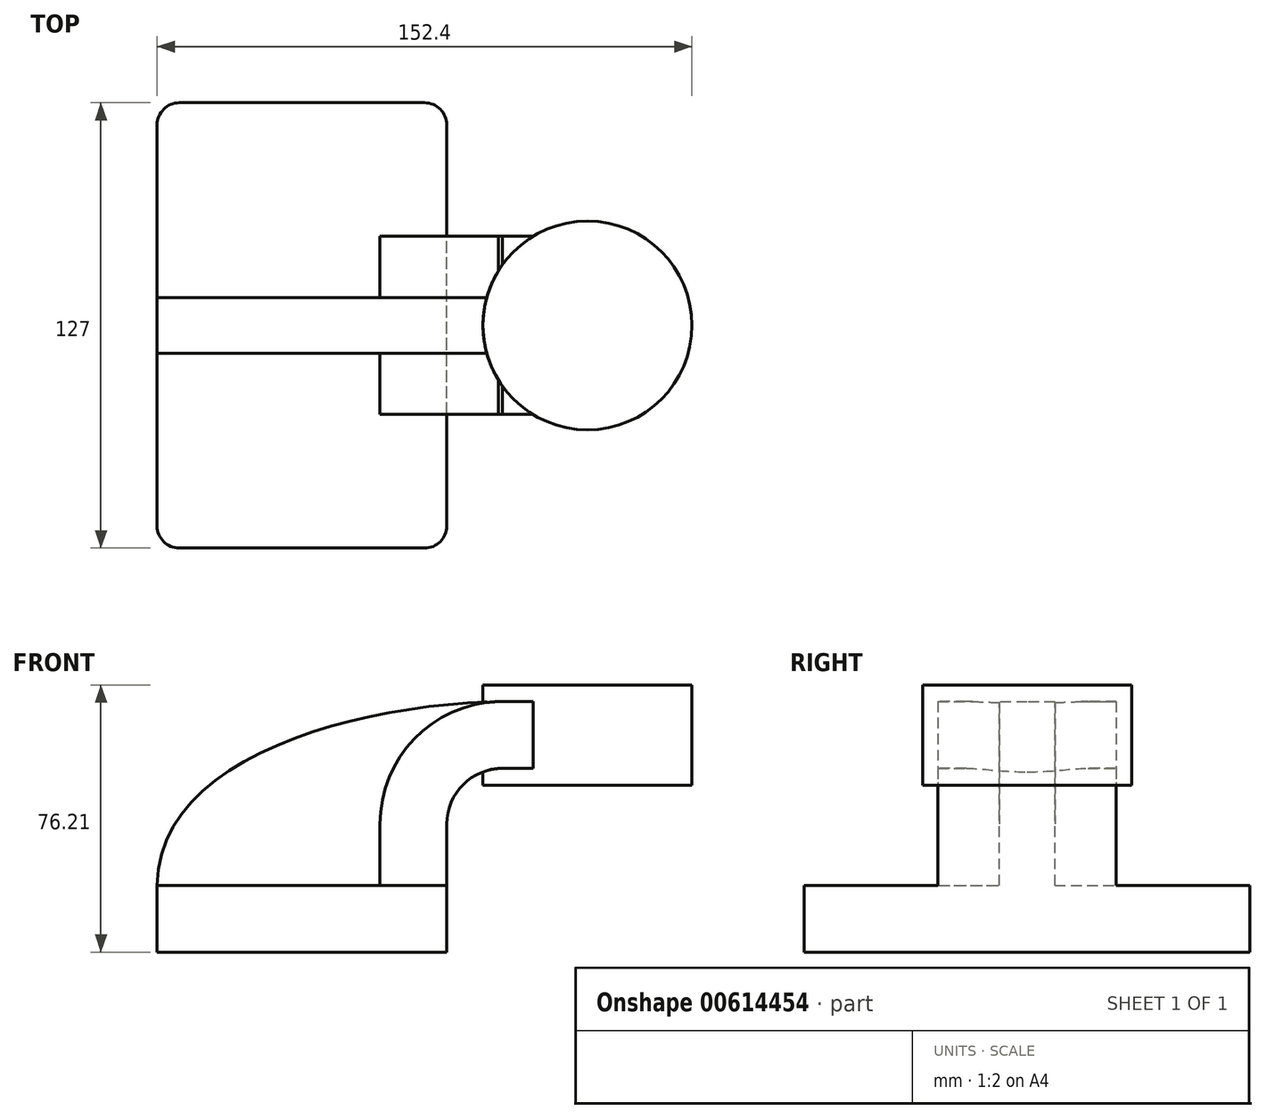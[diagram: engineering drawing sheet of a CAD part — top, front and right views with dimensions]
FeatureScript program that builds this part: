
annotation { "Feature Type Name" : "Feature", "Feature Type Description" : "" }
export const myFeature = defineFeature(function(context is Context, id is Id, definition is map)
    precondition{}
    {
        {
            var Q0;
            Q0=qCreatedBy(makeId("Front.planeOp"),FACE);
            var sketch = newSketch(context, id + "F0", { "sketchPlane" : qUnion([Q0])});
            skLineSegment(sketch, "E0.bottom", {"start": v(43.52, -9.53) * mm, "end": v(-39.03, -9.52) * mm});
            skLineSegment(sketch, "E0.top", {"start": v(43.52, 9.52) * mm, "end": v(-39.03, 9.53) * mm});
            skLineSegment(sketch, "E0.left", {"start": v(43.52, -9.53) * mm, "end": v(43.52, 9.52) * mm});
            skLineSegment(sketch, "E0.right", {"start": v(-39.03, -9.52) * mm, "end": v(-39.03, 9.53) * mm});
            skPoint(sketch, "E0.middle", {"position": v(2.24, 0) * mm});
            skLineSegment(sketch, "E1.bottom", {"start": v(62.57, 38.1) * mm, "end": v(113.37, 38.1) * mm});
            skLineSegment(sketch, "E1.top", {"start": v(62.57, 66.67) * mm, "end": v(113.37, 66.67) * mm});
            skLineSegment(sketch, "E1.left", {"start": v(62.57, 38.1) * mm, "end": v(62.57, 66.67) * mm});
            skLineSegment(sketch, "E1.right", {"start": v(113.37, 38.1) * mm, "end": v(113.37, 66.67) * mm});
            skPoint(sketch, "E1.middle", {"position": v(87.97, 52.39) * mm});
            skLineSegment(sketch, "E2", {"start": v(43.52, 9.52) * mm, "end": v(43.52, 27) * mm});
            skArc(sketch, "E3", {"start": v(43.52, 27) * mm, "mid": v(48.17, 38.23) * mm, "end": v(59.4, 42.88) * mm});
            skLineSegment(sketch, "E4", {"start": v(59.4, 42.88) * mm, "end": v(83.6, 42.88) * mm});
            skLineSegment(sketch, "E5.0", {"start": v(59.4, 61.93) * mm, "end": v(83.6, 61.93) * mm});
            skArc(sketch, "E5.1", {"start": v(24.47, 27) * mm, "mid": v(34.7, 51.7) * mm, "end": v(59.4, 61.93) * mm});
            skLineSegment(sketch, "E5.2", {"start": v(24.47, 9.52) * mm, "end": v(24.47, 27) * mm});
            skLineSegment(sketch, "E6", {"start": v(83.6, 38.1) * mm, "end": v(83.6, 66.67) * mm});
            skFitSpline(sketch, "E7", {"points": [v(-39.03, 9.53) * mm, v(59.4, 61.93) * mm], "startDerivative": vector(0.44, 109.88) * mm, "endDerivative": vector(124.48, 1.75) * mm});
            skSolve(sketch);
        }
        {
            var Q0;
            Q0=makeQuery(id+"F0.imprint","IMPRINT",FACE,{"disambiguationData":[TD([[makeQuery(id+"F0.imprint","IMPRINT",EDGE,{"derivedFrom":sQuery(id+"F0.wireOp",EDGE,"E0.bottom")}),-1.0]])]});
            extrude(context, id + "F1", {"entities" : qUnion([Q0]), "endBound" : BoundingType.SYMMETRIC, "depth" : (5 * 25.4) * mm, "offsetDistance" : 25 * mm});
        }
        {
            var Q0;
            {var subQ1=sQuery(id+"F0.wireOp",EDGE,"E2");Q0=makeQuery(id+"F0.imprint","IMPRINT",FACE,{"disambiguationData":[TD([[makeQuery(id+"F0.imprint","IMPRINT",EDGE,{"derivedFrom":subQ1}),1.0]])]});}
            var Q1;
            {var subQ0=sQuery(id+"F0.wireOp",EDGE,"E4");var subQ1=sQuery(id+"F0.wireOp",EDGE,"E1.left");var subQ2=makeQuery(id+"F0.imprint","INTERSECT",VERTEX,{"derivedFrom":[subQ1,subQ0]});Q1=makeQuery(id+"F0.imprint","IMPRINT",FACE,{"disambiguationData":[TD([[makeQuery(id+"F0.imprint","IMPRINT",EDGE,{"disambiguationData":[TD([[subQ2,-1.0]])],"derivedFrom":subQ1}),-1.0]])]});}
            extrude(context, id + "F2", {"entities" : qUnion([Q0, Q1]), "operationType" : NewBodyOperationType.ADD, "endBound" : BoundingType.SYMMETRIC, "depth" : (2 * 25.4) * mm, "offsetDistance" : 25 * mm});
        }
        {
            var Q0;
            {var subQ3=sQuery(id+"F0.wireOp",EDGE,"E5.2");Q0=makeQuery(id+"F0.imprint","IMPRINT",FACE,{"disambiguationData":[TD([[makeQuery(id+"F0.imprint","IMPRINT",EDGE,{"derivedFrom":subQ3}),1.0]])]});}
            extrude(context, id + "F3", {"entities" : qUnion([Q0]), "operationType" : NewBodyOperationType.ADD, "endBound" : BoundingType.SYMMETRIC, "depth" : (25.4 * 0.62) * mm, "offsetDistance" : 25 * mm});
        }
        {
            var Q0;
            {var subQ4=sQuery(id+"F0.wireOp",EDGE,"E1.right");Q0=makeQuery(id+"F0.imprint","IMPRINT",FACE,{"disambiguationData":[TD([[makeQuery(id+"F0.imprint","IMPRINT",EDGE,{"derivedFrom":subQ4}),1.0]])]});}
            var Q1;
            Q1=sQuery(id+"F0.wireOp",EDGE,"E6");
            revolve(context, id + "F4", {"operationType" : NewBodyOperationType.ADD, "entities" : qUnion([Q0]), "axis" : qUnion([Q1]), "revolveType" : RevolveType.FULL});
        }
        {
            var Q0;
            Q0=makeQuery(id+"F1.opExtrude","CAP_EDGE",EDGE,{"disambiguationData":[OSD([sQuery(id+"F0.wireOp",EDGE,"E0.right")])],"isStart":false});
            var Q1;
            Q1=makeQuery(id+"F1.opExtrude","CAP_EDGE",EDGE,{"disambiguationData":[OSD([sQuery(id+"F0.wireOp",EDGE,"E0.left")])],"isStart":false});
            var Q2;
            Q2=makeQuery(id+"F1.opExtrude","CAP_EDGE",EDGE,{"disambiguationData":[OSD([sQuery(id+"F0.wireOp",EDGE,"E0.left")])],"isStart":true});
            var Q3;
            Q3=makeQuery(id+"F1.opExtrude","CAP_EDGE",EDGE,{"disambiguationData":[OSD([sQuery(id+"F0.wireOp",EDGE,"E0.right")])],"isStart":true});
            fillet(context, id + "F5", {"entities" : qUnion([Q0, Q1, Q2, Q3]), "radius" : (25.4 * 0.25) * mm, "tangentPropagation" : true, "allowEdgeOverflow" : false});
        }
    });
